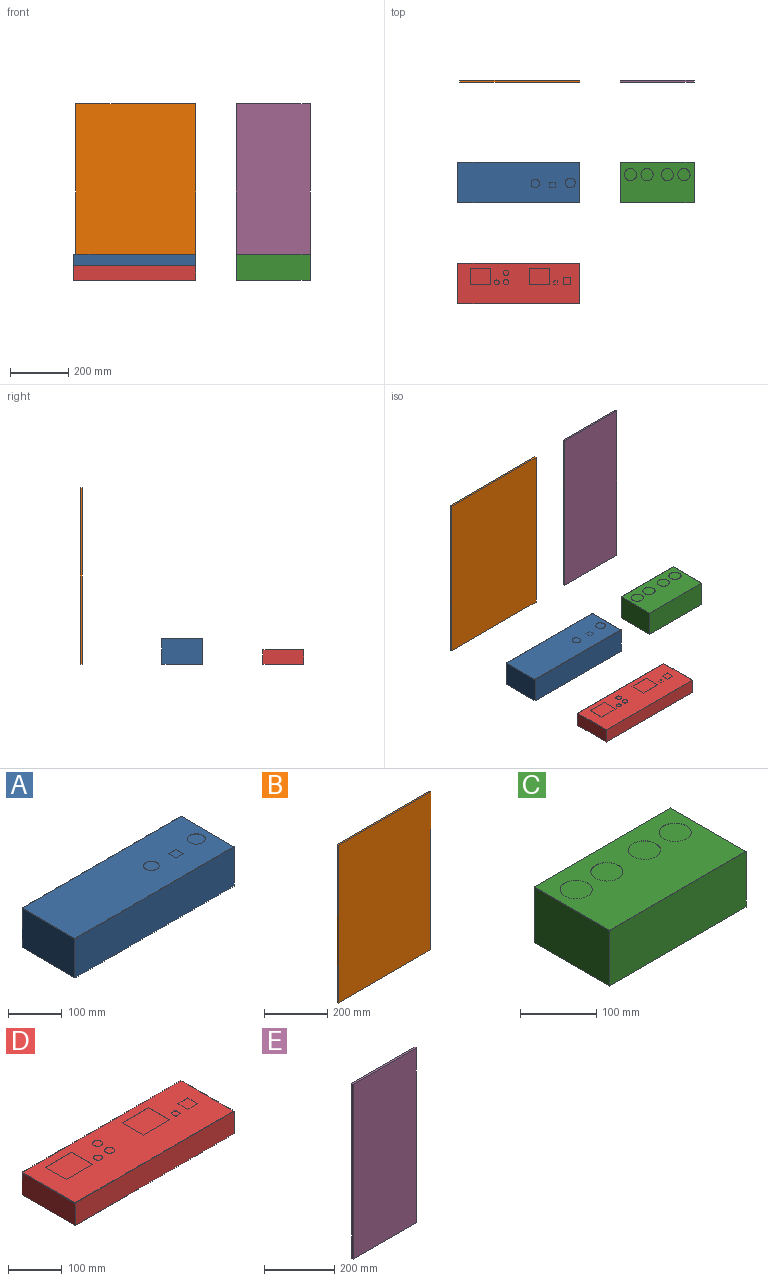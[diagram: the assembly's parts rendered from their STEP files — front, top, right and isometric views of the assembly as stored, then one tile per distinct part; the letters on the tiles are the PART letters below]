
ASSEMBLY  parts=5 mates=9
PART A: 32 faces, bbox 419.1x139.7x89.6 mm
  f0: plane 419.1x88.9mm, normal (0,1,0), area 37258mm2, adj f1,f7,f8,f9
  f1: plane 419.1x139.29mm, normal (0,0,1), area 58377.9mm2, adj f0,f2,f8,f9
  f2: plane 419.1x0.25mm, normal (0,1,0), area 106.5mm2, adj f1,f3,f8,f9
  f3: plane 419.1x139.29mm, normal (0,0,-1), area 56437.6mm2, adj f2,f4,f8,f9,f10,f11,f12,f13
  f4: plane 419.1x0.41mm, normal (0,1,0), area 170.3mm2, adj f3,f5,f8,f9
  f5: plane 419.1x139.7mm, normal (0,0,1), area 56608mm2, adj f4,f6,f8,f9,f10,f11,f12,f13
  f6: plane 419.1x89.56mm, normal (0,-1,0), area 37534.8mm2, adj f5,f7,f8,f9
  f7: plane 419.1x139.7mm, normal (0,0,-1), area 58548.3mm2, adj f0,f6,f8,f9
  f8: plane 139.7x89.56mm, normal (1,0,0), area 12476.2mm2, adj f0,f1,f2,f3,f4,f5,f6,f7
  f9: plane 139.7x89.56mm, normal (-1,0,0), area 12476.2mm2, adj f0,f1,f2,f3,f4,f5,f6,f7
  f10: extruded ~1.12x0.47mm, area 0.5mm2, adj f3,f5,f11,f19
  f11: plane 16.67x0.41mm, normal (0,-1,0), area 6.8mm2, adj f3,f5,f10,f12
  f12: extruded ~1.12x0.47mm, area 0.5mm2, adj f3,f5,f11,f13
  f13: extruded ~1.12x0.47mm, area 0.5mm2, adj f3,f5,f12,f14
  f14: plane 16.67x0.41mm, normal (1,0,0), area 6.8mm2, adj f3,f5,f13,f15
  f15: extruded ~1.12x0.47mm, area 0.5mm2, adj f3,f5,f14,f16
  f16: extruded ~1.12x0.47mm, area 0.5mm2, adj f3,f5,f15,f17
  f17: plane 16.67x0.41mm, normal (0,1,0), area 6.8mm2, adj f3,f5,f16,f18
  f18: extruded ~1.12x0.47mm, area 0.5mm2, adj f3,f5,f17,f20
  f19: extruded ~1.12x0.46mm, area 0.5mm2, adj f3,f5,f10,f21
  f20: extruded ~1.12x0.46mm, area 0.5mm2, adj f3,f5,f18,f21
  f21: plane 16.67x0.41mm, normal (-1,0,0), area 6.8mm2, adj f3,f5,f19,f20
  f22: extruded ~10.38x4.3mm, area 4.7mm2, adj f3,f5,f23,f24
  f23: extruded ~10.38x4.3mm, area 4.7mm2, adj f3,f5,f22,f25
  f24: extruded ~20.77x4.3mm, area 9.4mm2, adj f3,f5,f22,f26
  f25: extruded ~20.77x4.3mm, area 9.4mm2, adj f3,f5,f23,f26
  f26: extruded ~20.77x4.3mm, area 9.4mm2, adj f3,f5,f24,f25
  f27: extruded ~11.79x4.88mm, area 5.3mm2, adj f3,f5,f28,f29
  f28: extruded ~11.79x4.88mm, area 5.3mm2, adj f3,f5,f27,f30
  f29: extruded ~23.57x4.88mm, area 10.6mm2, adj f3,f5,f27,f31
  f30: extruded ~23.57x4.88mm, area 10.6mm2, adj f3,f5,f28,f31
  f31: extruded ~23.57x4.88mm, area 10.6mm2, adj f3,f5,f29,f30
PART B: 6 faces, bbox 412.8x6.4x609.6 mm
  f0: plane 609.6x6.35mm, normal (1,0,0), area 3871mm2, adj f1,f3,f4,f5
  f1: plane 412.75x6.35mm, normal (0,0,1), area 2621mm2, adj f0,f2,f4,f5
  f2: plane 609.6x6.35mm, normal (-1,0,0), area 3871mm2, adj f1,f3,f4,f5
  f3: plane 412.75x6.35mm, normal (0,0,-1), area 2621mm2, adj f0,f2,f4,f5
  f4: plane 609.6x412.75mm, normal (0,1,0), area 251612.4mm2, adj f0,f1,f2,f3
  f5: plane 609.6x412.75mm, normal (0,-1,0), area 251612.4mm2, adj f0,f1,f2,f3
PART C: 26 faces, bbox 254x139.7x89.6 mm
  f0: plane 254x88.9mm, normal (0,1,0), area 22580.6mm2, adj f1,f7,f8,f9
  f1: plane 254x139.29mm, normal (0,0,1), area 35380.6mm2, adj f0,f2,f8,f9
  f2: plane 254x0.25mm, normal (0,1,0), area 64.5mm2, adj f1,f3,f8,f9
  f3: plane 254x139.29mm, normal (0,0,-1), area 29826.2mm2, adj f2,f4,f8,f9,f10,f11,f12,f13
  f4: plane 254x0.41mm, normal (0,1,0), area 103.2mm2, adj f3,f5,f8,f9
  f5: plane 254x139.7mm, normal (0,0,1), area 29929.9mm2, adj f4,f6,f8,f9,f10,f11,f12,f13
  f6: plane 254x89.56mm, normal (0,-1,0), area 22748.3mm2, adj f5,f7,f8,f9
  f7: plane 254x139.7mm, normal (0,0,-1), area 35483.8mm2, adj f0,f6,f8,f9
  f8: plane 139.7x89.56mm, normal (1,0,0), area 12476.2mm2, adj f0,f1,f2,f3,f4,f5,f6,f7
  f9: plane 139.7x89.56mm, normal (-1,0,0), area 12476.2mm2, adj f0,f1,f2,f3,f4,f5,f6,f7
  f10: extruded ~35.91x21.03mm, area 20.1mm2, adj f3,f5,f11,f12
  f11: extruded ~29.75x6.16mm, area 13.4mm2, adj f3,f5,f10,f13
  f12: extruded ~14.87x6.16mm, area 6.7mm2, adj f3,f5,f10,f13
  f13: extruded ~29.75x6.16mm, area 13.4mm2, adj f3,f5,f11,f12
  f14: extruded ~35.91x21.03mm, area 20.1mm2, adj f3,f5,f15,f16
  f15: extruded ~29.75x6.16mm, area 13.4mm2, adj f3,f5,f14,f17
  f16: extruded ~14.87x6.16mm, area 6.7mm2, adj f3,f5,f14,f17
  f17: extruded ~29.75x6.16mm, area 13.4mm2, adj f3,f5,f15,f16
  f18: extruded ~35.91x21.03mm, area 20.1mm2, adj f3,f5,f19,f20
  f19: extruded ~29.75x6.16mm, area 13.4mm2, adj f3,f5,f18,f21
  f20: extruded ~14.87x6.16mm, area 6.7mm2, adj f3,f5,f18,f21
  f21: extruded ~29.75x6.16mm, area 13.4mm2, adj f3,f5,f19,f20
  f22: extruded ~35.91x21.03mm, area 20.1mm2, adj f3,f5,f23,f24
  f23: extruded ~29.75x6.16mm, area 13.4mm2, adj f3,f5,f22,f25
  f24: extruded ~14.87x6.16mm, area 6.7mm2, adj f3,f5,f22,f25
  f25: extruded ~29.75x6.16mm, area 13.4mm2, adj f3,f5,f23,f24
PART D: 49 faces, bbox 419.1x139.7x51.5 mm
  f0: plane 419.1x50.8mm, normal (0,1,0), area 21290.3mm2, adj f1,f7,f8,f9
  f1: plane 419.1x139.29mm, normal (0,0,1), area 58377.9mm2, adj f0,f2,f8,f9
  f2: plane 419.1x0.25mm, normal (0,1,0), area 106.5mm2, adj f1,f3,f8,f9
  f3: plane 419.1x139.29mm, normal (0,0,-1), area 48965mm2, adj f2,f4,f8,f9,f10,f11,f12,f13
  f4: plane 419.1x0.41mm, normal (0,1,0), area 170.3mm2, adj f3,f5,f8,f9
  f5: plane 419.1x139.7mm, normal (0,0,1), area 49135.5mm2, adj f4,f6,f8,f9,f10,f11,f12,f13
  f6: plane 419.1x51.46mm, normal (0,-1,0), area 21567.1mm2, adj f5,f7,f8,f9
  f7: plane 419.1x139.7mm, normal (0,0,-1), area 58548.3mm2, adj f0,f6,f8,f9
  f8: plane 139.7x51.46mm, normal (1,0,0), area 7153.6mm2, adj f0,f1,f2,f3,f4,f5,f6,f7
  f9: plane 139.7x51.46mm, normal (-1,0,0), area 7153.6mm2, adj f0,f1,f2,f3,f4,f5,f6,f7
  f10: extruded ~5.89x2.44mm, area 2.7mm2, adj f3,f5,f11,f12
  f11: extruded ~5.89x2.44mm, area 2.7mm2, adj f3,f5,f10,f13
  f12: extruded ~11.79x2.44mm, area 5.3mm2, adj f3,f5,f10,f14
  f13: extruded ~11.79x2.44mm, area 5.3mm2, adj f3,f5,f11,f14
  f14: extruded ~11.79x2.44mm, area 5.3mm2, adj f3,f5,f12,f13
  f15: plane 26.19x0.41mm, normal (-1,0,0), area 10.6mm2, adj f3,f5,f16,f17
  f16: plane 26.19x0.41mm, normal (0,1,0), area 10.6mm2, adj f3,f5,f15,f18
  f17: plane 26.19x0.41mm, normal (0,-1,0), area 10.6mm2, adj f3,f5,f15,f18
  f18: plane 26.19x0.41mm, normal (1,0,0), area 10.6mm2, adj f3,f5,f16,f17
  f19: extruded ~1.68x0.7mm, area 0.8mm2, adj f3,f5,f20,f28
  f20: plane 8.73x0.41mm, normal (0,-1,0), area 3.5mm2, adj f3,f5,f19,f21
  f21: extruded ~1.68x0.7mm, area 0.8mm2, adj f3,f5,f20,f22
  f22: extruded ~1.68x0.7mm, area 0.8mm2, adj f3,f5,f21,f23
  f23: plane 8.73x0.41mm, normal (1,0,0), area 3.5mm2, adj f3,f5,f22,f24
  f24: extruded ~1.68x0.7mm, area 0.8mm2, adj f3,f5,f23,f25
  f25: extruded ~1.68x0.7mm, area 0.8mm2, adj f3,f5,f24,f26
  f26: plane 8.73x0.41mm, normal (0,1,0), area 3.5mm2, adj f3,f5,f25,f27
  f27: extruded ~1.68x0.7mm, area 0.8mm2, adj f3,f5,f26,f29
  f28: extruded ~1.68x0.7mm, area 0.8mm2, adj f3,f5,f19,f30
  f29: extruded ~1.68x0.7mm, area 0.8mm2, adj f3,f5,f27,f30
  f30: plane 8.73x0.41mm, normal (-1,0,0), area 3.5mm2, adj f3,f5,f28,f29
  f31: plane 55.56x0.41mm, normal (-1,0,0), area 22.6mm2, adj f3,f5,f32,f33
  f32: plane 69.85x0.41mm, normal (0,1,0), area 28.4mm2, adj f3,f5,f31,f34
  f33: plane 69.85x0.41mm, normal (0,-1,0), area 28.4mm2, adj f3,f5,f31,f34
  f34: plane 55.56x0.41mm, normal (1,0,0), area 22.6mm2, adj f3,f5,f32,f33
  f35: extruded ~6.74x2.79mm, area 3mm2, adj f3,f5,f36,f37
  f36: extruded ~6.74x2.79mm, area 3mm2, adj f3,f5,f35,f38
  f37: extruded ~13.47x2.79mm, area 6.1mm2, adj f3,f5,f35,f39
  f38: extruded ~13.47x2.79mm, area 6.1mm2, adj f3,f5,f36,f39
  f39: extruded ~13.47x2.79mm, area 6.1mm2, adj f3,f5,f37,f38
  f40: extruded ~6.74x2.79mm, area 3mm2, adj f3,f5,f41,f42
  f41: extruded ~6.74x2.79mm, area 3mm2, adj f3,f5,f40,f43
  f42: extruded ~13.47x2.79mm, area 6.1mm2, adj f3,f5,f40,f44
  f43: extruded ~13.47x2.79mm, area 6.1mm2, adj f3,f5,f41,f44
  f44: extruded ~13.47x2.79mm, area 6.1mm2, adj f3,f5,f42,f43
  f45: plane 69.85x0.41mm, normal (0,1,0), area 28.4mm2, adj f3,f5,f46,f47
  f46: plane 55.56x0.41mm, normal (1,0,0), area 22.6mm2, adj f3,f5,f45,f48
  f47: plane 55.56x0.41mm, normal (-1,0,0), area 22.6mm2, adj f3,f5,f45,f48
  f48: plane 69.85x0.41mm, normal (0,-1,0), area 28.4mm2, adj f3,f5,f46,f47
PART E: 6 faces, bbox 254x6.4x609.6 mm
  f0: plane 609.6x6.35mm, normal (1,0,0), area 3871mm2, adj f1,f3,f4,f5
  f1: plane 254x6.35mm, normal (0,0,1), area 1612.9mm2, adj f0,f2,f4,f5
  f2: plane 609.6x6.35mm, normal (-1,0,0), area 3871mm2, adj f1,f3,f4,f5
  f3: plane 254x6.35mm, normal (0,0,-1), area 1612.9mm2, adj f0,f2,f4,f5
  f4: plane 609.6x254mm, normal (0,1,0), area 154838.4mm2, adj f0,f1,f2,f3
  f5: plane 609.6x254mm, normal (0,-1,0), area 154838.4mm2, adj f0,f1,f2,f3
PLACE A t=(-183.92,-187.67,-77.43)mm
PLACE B t=(25.63,86.65,-77.43)mm fixed
PLACE C t=(292.97,-187.67,-77.43)mm
PLACE D t=(-183.92,-535.65,-77.43)mm
PLACE E t=(419.97,86.65,-77.43)mm
MATE parallel A.f0 <-> B.f5  axis (0,1,0) through (-183.92,-187.67,11.47)mm
MATE parallel A.f6 <-> D.f0  axis (0,-1,0) through (-183.92,-327.37,-32.65)mm
MATE planar A.f8 <-> D.f8  axis (1,0,0) through (25.63,-257.52,-32.77)mm
MATE planar E.f2 <-> C.f9  axis (-1,0,0) through (165.97,89.82,227.37)mm
MATE planar A.f8 <-> B.f0  axis (1,0,0) through (25.63,-257.52,-32.77)mm
MATE parallel E.f5 <-> C.f0  axis (0,-1,0) through (292.97,86.65,227.37)mm
MATE planar B.f3 <-> A.f7  axis (0,0,-1) through (-180.74,89.82,-77.43)mm
MATE planar E.f3 <-> C.f7  axis (0,0,-1) through (292.97,89.82,-77.43)mm
MATE planar A.f7 <-> D.f7  axis (0,0,-1) through (-183.92,-257.52,-77.43)mm
